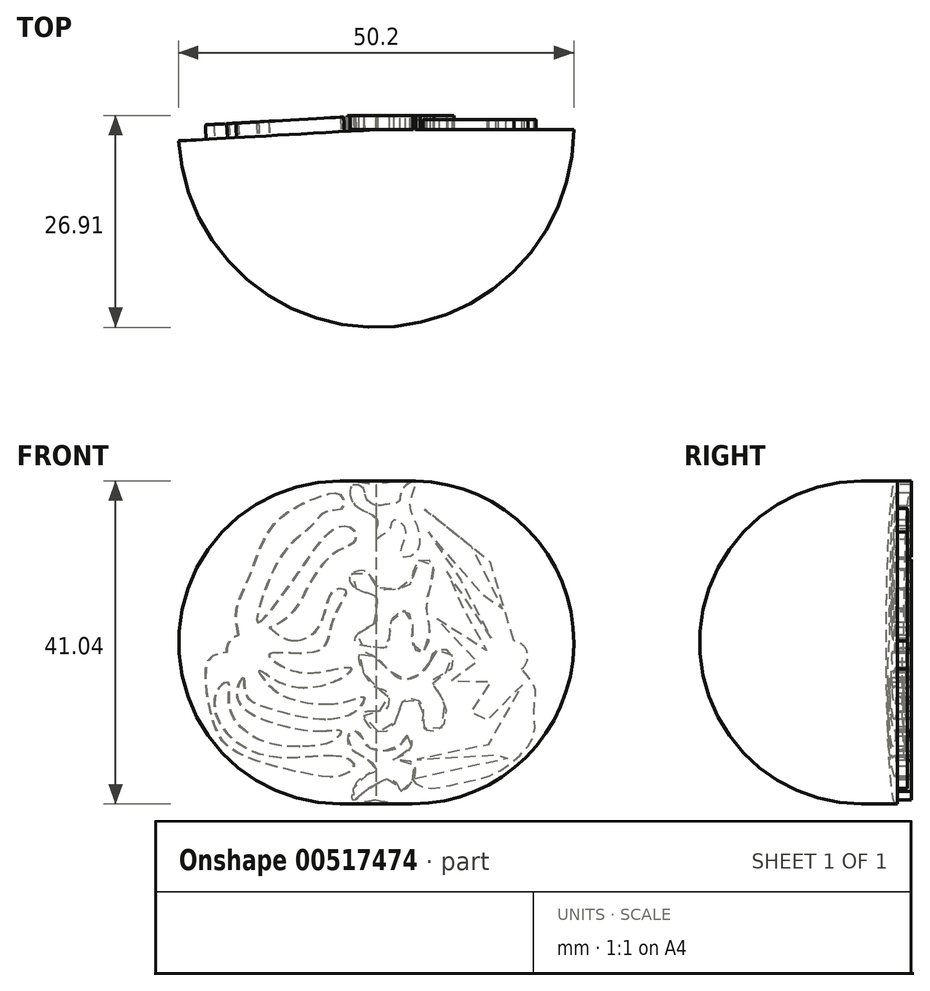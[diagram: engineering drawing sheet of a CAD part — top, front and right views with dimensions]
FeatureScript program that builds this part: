
annotation { "Feature Type Name" : "Feature", "Feature Type Description" : "" }
export const myFeature = defineFeature(function(context is Context, id is Id, definition is map)
    precondition{}
    {
        {
            var Q0;
            Q0=qCreatedBy(makeId("Front.planeOp"),FACE);
            var sketch = newSketch(context, id + "F0", { "sketchPlane" : qUnion([Q0])});
            skLineSegment(sketch, "E0", {"start": v(0, 40) * mm, "end": v(0, 0) * mm});
            skArc(sketch, "E1", {"start": v(0, 0) * mm, "mid": v(25.12, 20) * mm, "end": v(0, 40) * mm});
            skSolve(sketch);
        }
        {
            var Q0;
            Q0=makeQuery(id+"F0.imprint","IMPRINT",FACE,{"disambiguationData":[TD([[makeQuery(id+"F0.imprint","IMPRINT",EDGE,{"derivedFrom":sQuery(id+"F0.wireOp",EDGE,"E0")}),1.0]])]});
            var Q1;
            Q1=sQuery(id+"F0.wireOp",EDGE,"E0");
            revolve(context, id + "F1", {"entities" : qUnion([Q0]), "axis" : qUnion([Q1]), "revolveType" : RevolveType.ONE_DIRECTION, "angle" : 176.75 * degree});
        }
        {
            var Q0;
            Q0=makeQuery(id+"F1.opRevolve","CAP_FACE",FACE,{"disambiguationData":[OSD([sQuery(id+"F0.wireOp",EDGE,"E0"),sQuery(id+"F0.wireOp",EDGE,"E1")])],"isStart":true});
            var sketch = newSketch(context, id + "F2", { "sketchPlane" : qUnion([Q0])});
            skFitSpline(sketch, "E2", {"points": [v(-3.24, 39.33) * mm, v(-2.95, 37.93) * mm, v(-1.28, 37.52) * mm, v(0, 37.41) * mm, v(1.25, 38.3) * mm, v(1.64, 39.61) * mm, v(2.94, 39.96) * mm, v(3.32, 38.8) * mm, v(2.27, 37.14) * mm, v(0, 35.83) * mm, v(0, 34.44) * mm, v(1.22, 33.47) * mm, v(3.12, 32.5) * mm, v(2.5, 31.08) * mm, v(0, 31.44) * mm, v(0, 33.06) * mm, v(-1.8, 34.38) * mm, v(-2.09, 35.52) * mm, v(-3.2, 35.17) * mm, v(-3.7, 33.4) * mm, v(-3.12, 31.09) * mm, v(-5.11, 31.39) * mm, v(-5.2, 34.93) * mm, v(-4.35, 37.76) * mm, v(-5, 40.52) * mm, v(-3.24, 39.33) * mm]});
            skFitSpline(sketch, "E3", {"points": [v(-5.05, 30.08) * mm, v(-4.4, 27.45) * mm, v(-1.7, 26.66) * mm, v(0, 27.24) * mm, v(1.4, 29.03) * mm, v(3.32, 28.41) * mm, v(2.31, 26.73) * mm, v(0, 25.79) * mm, v(0, 24.01) * mm, v(0, 22.59) * mm, v(1.42, 21.76) * mm, v(2.74, 20.16) * mm, v(0, 19.41) * mm, v(-1.46, 19.45) * mm, v(-1.75, 21.1) * mm, v(-2.12, 23.07) * mm, v(-3.58, 24.08) * mm, v(-4.57, 22.72) * mm, v(-4.6, 20) * mm, v(-5.71, 18.6) * mm, v(-6.85, 20.9) * mm, v(-6.41, 24.8) * mm, v(-7.2, 27.98) * mm, v(-7, 30.29) * mm, v(-5.05, 30.08) * mm]});
            skFitSpline(sketch, "E4", {"points": [v(-6.85, 17.57) * mm, v(-5.85, 16.2) * mm, v(-4.3, 15.32) * mm, v(-2.63, 15.6) * mm, v(0, 18.03) * mm, v(1.96, 18.6) * mm, v(2.03, 17.1) * mm, v(0, 14.3) * mm, v(-1.3, 13.78) * mm, v(-1.17, 11.5) * mm, v(1.52, 11.04) * mm, v(0, 8.7) * mm, v(-2.52, 9.97) * mm, v(-3.52, 12.7) * mm, v(-5.27, 12.68) * mm, v(-6.06, 11.14) * mm, v(-5.81, 9.39) * mm, v(-7.92, 8.8) * mm, v(-8.7, 12.36) * mm, v(-7.25, 15.25) * mm, v(-9.64, 16.74) * mm, v(-9.13, 18.97) * mm, v(-7.34, 18.75) * mm, v(-6.85, 17.57) * mm]});
            skFitSpline(sketch, "E5", {"points": [v(-4, 8.15) * mm, v(-2.8, 6.72) * mm, v(0, 6.3) * mm, v(1.3, 7.02) * mm, v(2.12, 8.47) * mm, v(3.34, 8.53) * mm, v(3.41, 6.85) * mm, v(1.43, 5.37) * mm, v(0, 3.77) * mm, v(2.23, 2.48) * mm, v(2.95, 0) * mm, v(1.07, 1.4) * mm, v(0, 2.01) * mm, v(-1.67, 2.64) * mm, v(-2.9, 1.59) * mm, v(-3.06, 1.09) * mm, v(-4.68, 2.47) * mm, v(-4.44, 4.8) * mm, v(-2.2, 5.08) * mm, v(-4.49, 6.68) * mm, v(-4, 8.15) * mm]});
            skSolve(sketch);
        }
        {
            var Q0;
            {var subQ0=sQuery(id+"F2.wireOp",EDGE,"E5");var subQ1=makeQuery(id+"F1.opRevolve","CAP_EDGE",EDGE,{"disambiguationData":[OSD([sQuery(id+"F0.wireOp",EDGE,"E0")])],"isStart":true});var subQ2=makeQuery(id+"F2.imprint","INTERSECT",VERTEX,{"disambiguationData":[OD(0.0)],"derivedFrom":[subQ1,subQ0]});Q0=makeQuery(id+"F2.imprint","IMPRINT",FACE,{"disambiguationData":[TD([[makeQuery(id+"F2.imprint","IMPRINT",EDGE,{"disambiguationData":[TD([[subQ2,1.0]])],"derivedFrom":subQ0}),-1.0]])]});}
            var Q1;
            {var subQ0=sQuery(id+"F2.wireOp",EDGE,"E5");var subQ1=makeQuery(id+"F1.opRevolve","CAP_EDGE",EDGE,{"disambiguationData":[OSD([sQuery(id+"F0.wireOp",EDGE,"E0")])],"isStart":true});var subQ2=makeQuery(id+"F2.imprint","INTERSECT",VERTEX,{"disambiguationData":[OD(2.0)],"derivedFrom":[subQ1,subQ0]});Q1=makeQuery(id+"F2.imprint","IMPRINT",FACE,{"disambiguationData":[TD([[makeQuery(id+"F2.imprint","IMPRINT",EDGE,{"disambiguationData":[TD([[subQ2,-1.0]])],"derivedFrom":subQ0}),-1.0]])]});}
            var Q2;
            {var subQ0=sQuery(id+"F2.wireOp",EDGE,"E5");var subQ1=makeQuery(id+"F1.opRevolve","CAP_EDGE",EDGE,{"disambiguationData":[OSD([sQuery(id+"F0.wireOp",EDGE,"E0")])],"isStart":true});var subQ2=makeQuery(id+"F2.imprint","INTERSECT",VERTEX,{"disambiguationData":[OD(0.0)],"derivedFrom":[subQ1,subQ0]});Q2=makeQuery(id+"F2.imprint","IMPRINT",FACE,{"disambiguationData":[TD([[makeQuery(id+"F2.imprint","IMPRINT",EDGE,{"disambiguationData":[TD([[subQ2,-1.0]])],"derivedFrom":subQ0}),-1.0]])]});}
            var Q3;
            {var subQ0=sQuery(id+"F2.wireOp",EDGE,"E4");var subQ1=makeQuery(id+"F1.opRevolve","CAP_EDGE",EDGE,{"disambiguationData":[OSD([sQuery(id+"F0.wireOp",EDGE,"E0")])],"isStart":true});var subQ2=makeQuery(id+"F2.imprint","INTERSECT",VERTEX,{"disambiguationData":[OD(0.0)],"derivedFrom":[subQ1,subQ0]});Q3=makeQuery(id+"F2.imprint","IMPRINT",FACE,{"disambiguationData":[TD([[makeQuery(id+"F2.imprint","IMPRINT",EDGE,{"disambiguationData":[TD([[subQ2,-1.0]])],"derivedFrom":subQ0}),-1.0]])]});}
            var Q4;
            {var subQ0=sQuery(id+"F2.wireOp",EDGE,"E4");var subQ1=makeQuery(id+"F1.opRevolve","CAP_EDGE",EDGE,{"disambiguationData":[OSD([sQuery(id+"F0.wireOp",EDGE,"E0")])],"isStart":true});var subQ2=makeQuery(id+"F2.imprint","INTERSECT",VERTEX,{"disambiguationData":[OD(0.0)],"derivedFrom":[subQ1,subQ0]});Q4=makeQuery(id+"F2.imprint","IMPRINT",FACE,{"disambiguationData":[TD([[makeQuery(id+"F2.imprint","IMPRINT",EDGE,{"disambiguationData":[TD([[subQ2,1.0]])],"derivedFrom":subQ0}),-1.0]])]});}
            var Q5;
            {var subQ0=sQuery(id+"F2.wireOp",EDGE,"E4");var subQ1=makeQuery(id+"F1.opRevolve","CAP_EDGE",EDGE,{"disambiguationData":[OSD([sQuery(id+"F0.wireOp",EDGE,"E0")])],"isStart":true});var subQ2=makeQuery(id+"F2.imprint","INTERSECT",VERTEX,{"disambiguationData":[OD(2.0)],"derivedFrom":[subQ1,subQ0]});Q5=makeQuery(id+"F2.imprint","IMPRINT",FACE,{"disambiguationData":[TD([[makeQuery(id+"F2.imprint","IMPRINT",EDGE,{"disambiguationData":[TD([[subQ2,-1.0]])],"derivedFrom":subQ0}),-1.0]])]});}
            var Q6;
            {var subQ0=sQuery(id+"F2.wireOp",EDGE,"E3");var subQ1=makeQuery(id+"F1.opRevolve","CAP_EDGE",EDGE,{"disambiguationData":[OSD([sQuery(id+"F0.wireOp",EDGE,"E0")])],"isStart":true});var subQ2=makeQuery(id+"F2.imprint","INTERSECT",VERTEX,{"disambiguationData":[OD(0.0)],"derivedFrom":[subQ1,subQ0]});Q6=makeQuery(id+"F2.imprint","IMPRINT",FACE,{"disambiguationData":[TD([[makeQuery(id+"F2.imprint","IMPRINT",EDGE,{"disambiguationData":[TD([[subQ2,-1.0]])],"derivedFrom":subQ0}),-1.0]])]});}
            var Q7;
            {var subQ0=sQuery(id+"F2.wireOp",EDGE,"E3");var subQ1=makeQuery(id+"F1.opRevolve","CAP_EDGE",EDGE,{"disambiguationData":[OSD([sQuery(id+"F0.wireOp",EDGE,"E0")])],"isStart":true});var subQ2=makeQuery(id+"F2.imprint","INTERSECT",VERTEX,{"disambiguationData":[OD(4.0)],"derivedFrom":[subQ1,subQ0]});Q7=makeQuery(id+"F2.imprint","IMPRINT",FACE,{"disambiguationData":[TD([[makeQuery(id+"F2.imprint","IMPRINT",EDGE,{"disambiguationData":[TD([[subQ2,-1.0]])],"derivedFrom":subQ0}),-1.0]])]});}
            var Q8;
            {var subQ0=sQuery(id+"F2.wireOp",EDGE,"E3");var subQ1=makeQuery(id+"F1.opRevolve","CAP_EDGE",EDGE,{"disambiguationData":[OSD([sQuery(id+"F0.wireOp",EDGE,"E0")])],"isStart":true});var subQ2=makeQuery(id+"F2.imprint","INTERSECT",VERTEX,{"disambiguationData":[OD(0.0)],"derivedFrom":[subQ1,subQ0]});Q8=makeQuery(id+"F2.imprint","IMPRINT",FACE,{"disambiguationData":[TD([[makeQuery(id+"F2.imprint","IMPRINT",EDGE,{"disambiguationData":[TD([[subQ2,1.0]])],"derivedFrom":subQ0}),-1.0]])]});}
            var Q9;
            {var subQ0=sQuery(id+"F2.wireOp",EDGE,"E2");var subQ1=makeQuery(id+"F1.opRevolve","CAP_EDGE",EDGE,{"disambiguationData":[OSD([sQuery(id+"F0.wireOp",EDGE,"E0")])],"isStart":true});var subQ7=makeQuery(id+"F2.imprint","INTERSECT",VERTEX,{"disambiguationData":[OD(0.0)],"derivedFrom":[subQ1,subQ0]});Q9=makeQuery(id+"F2.imprint","IMPRINT",FACE,{"disambiguationData":[TD([[makeQuery(id+"F2.imprint","IMPRINT",EDGE,{"disambiguationData":[TD([[subQ7,-1.0]])],"derivedFrom":subQ0}),-1.0]])]});}
            var Q10;
            {var subQ0=sQuery(id+"F2.wireOp",EDGE,"E2");var subQ1=makeQuery(id+"F1.opRevolve","CAP_EDGE",EDGE,{"disambiguationData":[OSD([sQuery(id+"F0.wireOp",EDGE,"E0")])],"isStart":true});var subQ2=makeQuery(id+"F2.imprint","INTERSECT",VERTEX,{"disambiguationData":[OD(0.0)],"derivedFrom":[subQ1,subQ0]});Q10=makeQuery(id+"F2.imprint","IMPRINT",FACE,{"disambiguationData":[TD([[makeQuery(id+"F2.imprint","IMPRINT",EDGE,{"disambiguationData":[TD([[subQ2,1.0]])],"derivedFrom":subQ0}),-1.0]])]});}
            extrude(context, id + "F3", {"entities" : qUnion([Q0, Q1, Q2, Q3, Q4, Q5, Q6, Q7, Q8, Q9, Q10]), "operationType" : NewBodyOperationType.ADD, "depth" : 1.8 * mm, "offsetDistance" : 25 * mm});
        }
        {
            var Q0;
            {var subQ0=sQuery(id+"F0.wireOp",EDGE,"E1");var subQ1=sQuery(id+"F2.wireOp",EDGE,"E5");var subQ2=sQuery(id+"F2.wireOp",EDGE,"E4");var subQ3=sQuery(id+"F2.wireOp",EDGE,"E3");var subQ4=sQuery(id+"F0.wireOp",EDGE,"E0");var subQ5=sQuery(id+"F2.wireOp",EDGE,"E2");var subQ6=makeQuery(id+"F1.opRevolve","CAP_EDGE",EDGE,{"disambiguationData":[OSD([subQ4])],"isStart":true});Q0=makeQuery(id+"F3.boolean.opBoolean","SPLIT",FACE,{"disambiguationData":[TD([makeQuery(id+"F1.opRevolve","CAP_FACE",FACE,{"disambiguationData":[OSD([subQ4,subQ0])],"isStart":false}),makeQuery(id+"F1.opRevolve","SWEPT_FACE",FACE,{"disambiguationData":[OSD([subQ0])]}),makeQuery(id+"F3.opExtrude","SWEPT_FACE",FACE,{"disambiguationData":[OSD([subQ5]),TDD([makeQuery(id+"F2.imprint","IMPRINT",EDGE,{"disambiguationData":[TD([[makeQuery(id+"F2.imprint","INTERSECT",VERTEX,{"disambiguationData":[OD(0.0)],"derivedFrom":[makeQuery(id+"F1.opRevolve","CAP_EDGE",EDGE,{"disambiguationData":[OSD([subQ0])],"isStart":true}),subQ5]}),1.0]])],"derivedFrom":subQ5})])]}),makeQuery(id+"F3.opExtrude","SWEPT_FACE",FACE,{"disambiguationData":[OSD([subQ3])]}),makeQuery(id+"F3.opExtrude","CAP_FACE",FACE,{"disambiguationData":[OSD([subQ4,subQ3])],"isStart":true}),makeQuery(id+"F3.opExtrude","SWEPT_FACE",FACE,{"disambiguationData":[OSD([subQ2])]}),makeQuery(id+"F3.opExtrude","CAP_FACE",FACE,{"disambiguationData":[OSD([subQ2])],"isStart":true}),makeQuery(id+"F3.opExtrude","SWEPT_FACE",FACE,{"disambiguationData":[OSD([subQ1])]}),makeQuery(id+"F3.opExtrude","CAP_FACE",FACE,{"disambiguationData":[OSD([subQ1])],"isStart":true}),makeQuery(id+"F3.opExtrude","SWEPT_FACE",FACE,{"disambiguationData":[OSD([subQ0])]}),makeQuery(id+"F3.opExtrude","SWEPT_FACE",FACE,{"disambiguationData":[OSD([subQ4]),TDD([makeQuery(id+"F2.imprint","IMPRINT",EDGE,{"disambiguationData":[TD([[makeQuery(id+"F2.imprint","INTERSECT",VERTEX,{"disambiguationData":[OD(2.0)],"derivedFrom":[subQ6,subQ5]}),-1.0]])],"derivedFrom":subQ6})])]})])],"derivedFrom":makeQuery(id+"F1.opRevolve","CAP_FACE",FACE,{"disambiguationData":[OSD([subQ4,subQ0])],"isStart":true})});}
            var sketch = newSketch(context, id + "F4", { "sketchPlane" : qUnion([Q0])});
            skCircle(sketch, "E6", {"center": v(-17.27, 18.2) * mm, "radius": 2 * mm});
            skFitSpline(sketch, "E7", {"points": [v(-17.5, 20.2) * mm, v(-17, 22.57) * mm, v(-16.73, 24.8) * mm, v(-15.43, 28.6) * mm, v(-13.41, 31.8) * mm, v(-10.82, 34.92) * mm, v(-7.82, 36.87) * mm, v(-6, 36.76) * mm, v(-6.66, 36.03) * mm, v(-8.14, 35.42) * mm, v(-9.73, 34.21) * mm, v(-11.34, 32.92) * mm, v(-13.37, 30.83) * mm, v(-14.3, 29.03) * mm, v(-15.41, 26.69) * mm, v(-15.93, 24.98) * mm, v(-16.37, 22.3) * mm, v(-16.37, 21) * mm, v(-15.41, 21.5) * mm, v(-14.07, 24.96) * mm, v(-12.39, 27.82) * mm, v(-9.9, 31.8) * mm, v(-8.09, 33.53) * mm, v(-6.57, 33.96) * mm, v(-6.57, 33.05) * mm, v(-7.57, 32.35) * mm, v(-9.55, 31.03) * mm, v(-10.3, 28.92) * mm, v(-11.5, 26.82) * mm, v(-13.2, 24.46) * mm, v(-14.16, 22.69) * mm, v(-15.18, 20.87) * mm, v(-14.07, 20.7) * mm, v(-13.27, 22.28) * mm, v(-11.6, 25.46) * mm, v(-9.34, 28.6) * mm, v(-8.52, 29.42) * mm, v(-8.23, 29.1) * mm, v(-8.04, 28.42) * mm, v(-8.54, 27.69) * mm, v(-9.66, 25.98) * mm, v(-11.1, 24.3) * mm, v(-11.8, 22.5) * mm, v(-12.55, 21.2) * mm, v(-13.3, 20.68) * mm, v(-13.55, 19.57) * mm, v(-14.18, 18.93) * mm, v(-12.52, 19.84) * mm, v(-10.14, 22.64) * mm, v(-7.68, 24.35) * mm, v(-7.61, 23.1) * mm, v(-8.77, 22.53) * mm, v(-9.61, 21.39) * mm, v(-10.68, 20.2) * mm, v(-11.61, 18.48) * mm, v(-13.11, 17.5) * mm, v(-14.32, 17.55) * mm, v(-13.93, 16.48) * mm, v(-12.82, 15.55) * mm, v(-11.43, 15.18) * mm, v(-9.34, 15.02) * mm, v(-9.2, 14.32) * mm, v(-9.7, 13.66) * mm, v(-10.84, 13.7) * mm, v(-13.3, 14.11) * mm, v(-14.43, 14.8) * mm, v(-14.96, 15.61) * mm, v(-15.37, 14.45) * mm, v(-15.51, 13.49) * mm, v(-14.63, 12.31) * mm, v(-12.57, 11.25) * mm, v(-10.74, 11.2) * mm, v(-9.99, 10.7) * mm, v(-9.76, 9.5) * mm, v(-11.03, 9.44) * mm, v(-14.1, 10.16) * mm, v(-16.15, 11.04) * mm, v(-16.87, 12) * mm, v(-17.35, 13.94) * mm, v(-17.89, 15.14) * mm, v(-18.68, 14.46) * mm, v(-18.73, 12.97) * mm, v(-17.94, 10.14) * mm, v(-16.53, 8.5) * mm, v(-13.32, 6.65) * mm, v(-10.06, 6.42) * mm, v(-7.45, 6.33) * mm, v(-5.12, 5.63) * mm, v(-5.73, 4.6) * mm, v(-8.22, 4.34) * mm, v(-11.96, 4.66) * mm, v(-15.24, 5.7) * mm, v(-17.53, 7.17) * mm, v(-18.68, 9) * mm, v(-18.73, 7.3) * mm, v(-16.08, 4.93) * mm, v(-11.23, 3.19) * mm, v(-6.73, 3) * mm, v(-4.72, 2.54) * mm, v(-6.23, 1.56) * mm, v(-10.6, 2.12) * mm, v(-15.29, 3.46) * mm, v(-20, 8.1) * mm, v(-20.04, 11.38) * mm, v(-20.27, 13.9) * mm, v(-18.48, 16.62) * mm], "startDerivative": vector(56.99, 236.84) * mm, "endDerivative": vector(203.12, 226.9) * mm});
            skSolve(sketch);
        }
        {
            var Q0;
            {var subQ0=sQuery(id+"F4.wireOp",EDGE,"E7");var subQ1=sQuery(id+"F4.wireOp",EDGE,"E6");var subQ2=makeQuery(id+"F4.imprint","INTERSECT",VERTEX,{"disambiguationData":[OD(0.0)],"derivedFrom":[subQ1,subQ0]});Q0=makeQuery(id+"F4.imprint","IMPRINT",FACE,{"disambiguationData":[TD([[makeQuery(id+"F4.imprint","IMPRINT",EDGE,{"disambiguationData":[TD([[subQ2,-1.0]])],"derivedFrom":subQ1}),1.0]])]});}
            var Q1;
            {var subQ0=sQuery(id+"F4.wireOp",EDGE,"E7");var subQ1=sQuery(id+"F4.wireOp",EDGE,"E6");var subQ2=makeQuery(id+"F4.imprint","INTERSECT",VERTEX,{"disambiguationData":[OD(0.0)],"derivedFrom":[subQ1,subQ0]});Q1=makeQuery(id+"F4.imprint","IMPRINT",FACE,{"disambiguationData":[TD([[makeQuery(id+"F4.imprint","IMPRINT",EDGE,{"disambiguationData":[TD([[subQ2,1.0]])],"derivedFrom":subQ1}),-1.0]])]});}
            extrude(context, id + "F5", {"entities" : qUnion([Q0, Q1]), "operationType" : NewBodyOperationType.ADD, "depth" : 1.28 * mm, "offsetDistance" : 25 * mm});
        }
        {
            var Q0;
            Q0=makeQuery(id+"F1.opRevolve","CAP_FACE",FACE,{"disambiguationData":[OSD([sQuery(id+"F0.wireOp",EDGE,"E0"),sQuery(id+"F0.wireOp",EDGE,"E1")])],"isStart":false});
            var sketch = newSketch(context, id + "F6", { "sketchPlane" : qUnion([Q0])});
            skCircle(sketch, "E8", {"center": v(16.91, 19.02) * mm, "radius": 2 * mm});
            skFitSpline(sketch, "E9", {"points": [v(17.43, 20.95) * mm, v(17.67, 24.24) * mm, v(15.95, 28.63) * mm, v(12.7, 35.25) * mm, v(6.58, 38.7) * mm, v(4.41, 38.7) * mm, v(4.2, 37.08) * mm, v(6.24, 36.67) * mm, v(7.96, 35.02) * mm, v(10.87, 32.41) * mm, v(13.04, 29.1) * mm, v(14.53, 25.36) * mm, v(15, 22.55) * mm, v(11.25, 26.84) * mm, v(8.27, 31.1) * mm, v(5.05, 34.54) * mm, v(2.96, 34.47) * mm, v(2.59, 33.02) * mm, v(3.63, 32.14) * mm, v(5.5, 31.16) * mm, v(8.34, 27.58) * mm, v(9.93, 24.68) * mm, v(11.96, 22.62) * mm, v(13.51, 21.91) * mm], "startDerivative": vector(14.97, 75.26) * mm, "endDerivative": vector(48.66, -16.86) * mm});
            skFitSpline(sketch, "E10", {"points": [v(13.51, 21.91) * mm, v(10.74, 20.26) * mm, v(7.25, 21.91) * mm, v(5.36, 26.5) * mm, v(3.87, 26.67) * mm, v(4.34, 25.12) * mm, v(5.73, 21.91) * mm, v(7.39, 18.87) * mm, v(13.51, 18.5) * mm, v(10.13, 16.3) * mm, v(4.28, 16.78) * mm, v(3.13, 16.68) * mm, v(4.55, 15.32) * mm, v(10, 14.24) * mm, v(13.51, 15.66) * mm, v(14.83, 16.37) * mm, v(13.51, 14.51) * mm, v(10.2, 12.66) * mm, v(3.94, 12.42) * mm, v(1.5, 13.03) * mm, v(2.55, 11.24) * mm, v(7.8, 10.3) * mm, v(13.51, 11.58) * mm, v(16.45, 13.4) * mm, v(16.83, 15.5) * mm, v(17.67, 13.26) * mm, v(13.51, 9.92) * mm, v(6.48, 8.77) * mm, v(4.45, 8.74) * mm, v(5.4, 7.52) * mm, v(10, 6.78) * mm, v(14.8, 7.62) * mm, v(18.55, 11.64) * mm, v(18.76, 14.89) * mm, v(20.07, 14.04) * mm, v(19.9, 9.85) * mm, v(13.51, 5.56) * mm, v(4.65, 5.56) * mm, v(2.79, 4.38) * mm, v(4.45, 3.07) * mm, v(8.67, 3.3) * mm, v(13.51, 4.45) * mm, v(18.86, 6.85) * mm, v(20.99, 11.14) * mm, v(21.22, 17.76) * mm, v(18.9, 18.78) * mm], "startDerivative": vector(-122.28, -109.23) * mm, "endDerivative": vector(-152.2, 18.52) * mm});
            skSolve(sketch);
        }
        {
            var Q0;
            {var subQ0=sQuery(id+"F6.wireOp",EDGE,"E8");var subQ1=makeQuery(id+"F6.imprint","INTERSECT",VERTEX,{"derivedFrom":[subQ0,sQuery(id+"F6.wireOp",EDGE,"E9")]});Q0=makeQuery(id+"F6.imprint","IMPRINT",FACE,{"disambiguationData":[TD([[makeQuery(id+"F6.imprint","IMPRINT",EDGE,{"disambiguationData":[TD([[subQ1,-1.0]])],"derivedFrom":subQ0}),1.0]])]});}
            var Q1;
            {var subQ0=sQuery(id+"F6.wireOp",EDGE,"E9");Q1=makeQuery(id+"F6.imprint","IMPRINT",FACE,{"disambiguationData":[TD([[makeQuery(id+"F6.imprint","IMPRINT",EDGE,{"derivedFrom":subQ0}),1.0]])]});}
            extrude(context, id + "F7", {"entities" : qUnion([Q0, Q1]), "operationType" : NewBodyOperationType.ADD, "depth" : 1.84 * mm, "offsetDistance" : 25 * mm});
        }
    });
